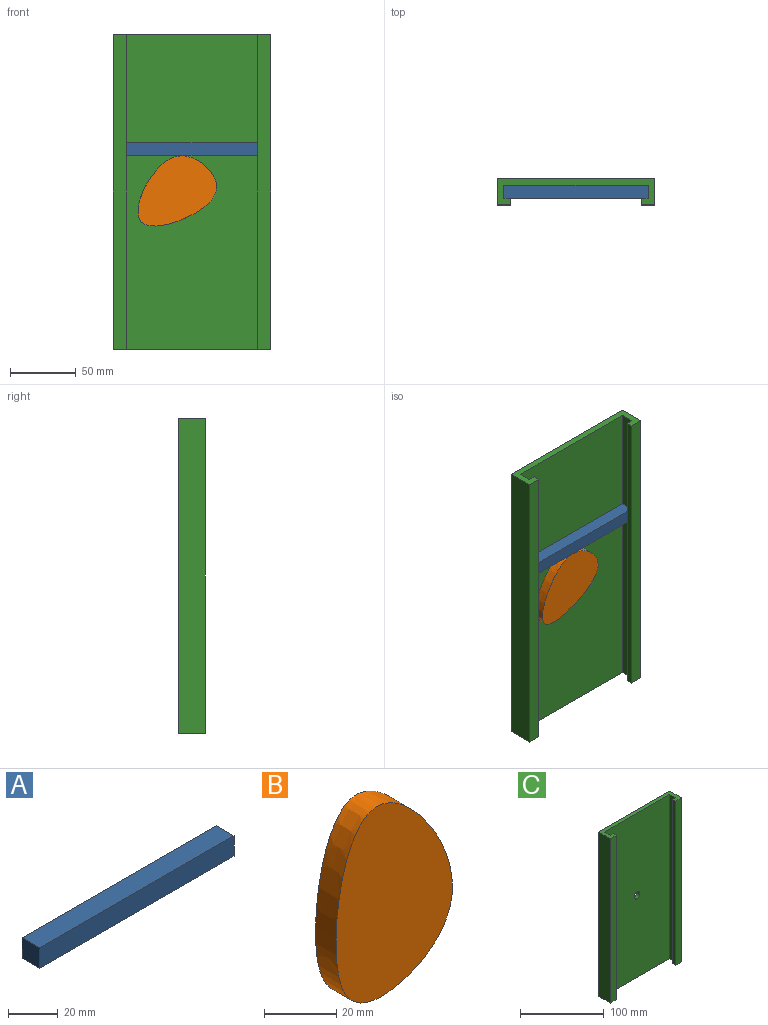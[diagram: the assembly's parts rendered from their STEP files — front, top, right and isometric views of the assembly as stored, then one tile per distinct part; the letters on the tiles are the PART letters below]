
ASSEMBLY  parts=3 mates=2
PART A: 6 faces, bbox 110x10x10 mm
  f0: plane 10x10mm, normal (1,0,0), area 100mm2, adj f1,f2,f4,f5
  f1: plane 110x10mm, normal (0,0,1), area 1100mm2, adj f0,f3,f4,f5
  f2: plane 110x10mm, normal (0,0,-1), area 1100mm2, adj f0,f3,f4,f5
  f3: plane 10x10mm, normal (-1,0,0), area 100mm2, adj f1,f2,f4,f5
  f4: plane 110x10mm, normal (0,1,0), area 1100mm2, adj f0,f1,f2,f3
  f5: plane 110x10mm, normal (0,-1,0), area 1100mm2, adj f0,f1,f2,f3
PART B: 5 faces, bbox 51x15x69 mm
  f0: plane 10x10mm, normal (0,1,0), area 78.5mm2, adj f1
  f1: cylinder r=5mm len=10mm, axis (0,-1,0), area 219.9mm2, adj f0,f4
  f2: extruded ~65.1x45.46mm, area 1405.8mm2, adj f3,f4
  f3: plane 69.02x51.05mm, normal (0,-1,0), area 2271.9mm2, adj f2
  f4: plane 69.02x51.05mm, normal (0,1,0), area 2193.4mm2, adj f1,f2
PART C: 15 faces, bbox 120x20x240 mm
  f0: plane 240x5mm, normal (1,0,0), area 1200mm2, adj f1,f3,f8,f13
  f1: plane 120x20mm, normal (0,0,-1), area 800mm2, adj f0,f2,f4,f5,f6,f7,f8,f9
  f2: plane 240x5mm, normal (-1,0,0), area 1200mm2, adj f1,f3,f6,f11
  f3: plane 120x20mm, normal (0,0,1), area 800mm2, adj f0,f2,f4,f5,f6,f7,f8,f9
  f4: plane 240x110mm, normal (0,-1,0), area 26321.5mm2, adj f1,f3,f5,f7,f14
  f5: plane 240x10mm, normal (-1,0,0), area 2400mm2, adj f1,f3,f4,f6
  f6: plane 240x5mm, normal (0,1,0), area 1200mm2, adj f1,f2,f3,f5
  f7: plane 240x10mm, normal (1,0,0), area 2400mm2, adj f1,f3,f4,f8
  f8: plane 240x5mm, normal (0,1,0), area 1200mm2, adj f0,f1,f3,f7
  f9: plane 240x120mm, normal (0,1,0), area 28721.5mm2, adj f1,f3,f10,f12,f14
  f10: plane 240x20mm, normal (1,0,0), area 4800mm2, adj f1,f3,f9,f11
  f11: plane 240x10mm, normal (0,-1,0), area 2400mm2, adj f1,f2,f3,f10
  f12: plane 240x20mm, normal (-1,0,0), area 4800mm2, adj f1,f3,f9,f13
  f13: plane 240x10mm, normal (0,-1,0), area 2400mm2, adj f0,f1,f3,f12
  f14: cylinder r=5mm len=10mm, axis (0,-1,0), area 157.1mm2, adj f4,f9
PLACE A t=(0,0,-82.47)mm
PLACE B rot(axis=(0,-1,0),118.8deg) t=(53.07,0,-96.35)mm
PLACE C at identity fixed
MATE revolute B.f1 <-> C.f14  axis (0,1,0) through (0,7,0)mm
MATE slider C.f3 <-> A.f1  axis (0,0,1) through (-55,2,120)mm
